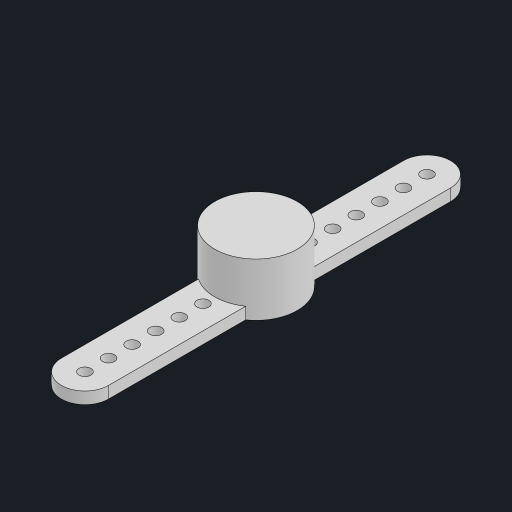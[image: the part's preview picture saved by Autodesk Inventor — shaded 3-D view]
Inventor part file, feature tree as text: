
AUTODESK INVENTOR PART (.ipt)
format: ipt  version: 2023 (Build 270158000, 158)  size: 133,120 bytes
history: native  units: in
note: dims shown in document units (in); Inventor stores cm internally (conversion verified against a paired STEP export)
features: sketch x3, extrude x2, other x1, hole x1, mirror x1
ambient origin geometry x8: Origin, YZ Plane, XZ Plane, XY Plane, X Axis, Y Axis, Z Axis, Center Point
bodies: Body1 (feature_tree)
feature tree (8):
  other  "ソリッド1"
  sketch  "スケッチ1"
  extrude  "押し出し1"  Depth=0.2756in
  extrude  "押し出し2"  Depth=0.1575in
  hole  "穴1"  [1 undecoded]
  mirror  "ミラー1"
  sketch  "スケッチ2"
  sketch  "スケッチ3"
note: 1 required parameter value undecoded (feature->parameter linkage not recoverable at this tier; creation-order binding heuristic only, values carry confidence <= 0.55)
